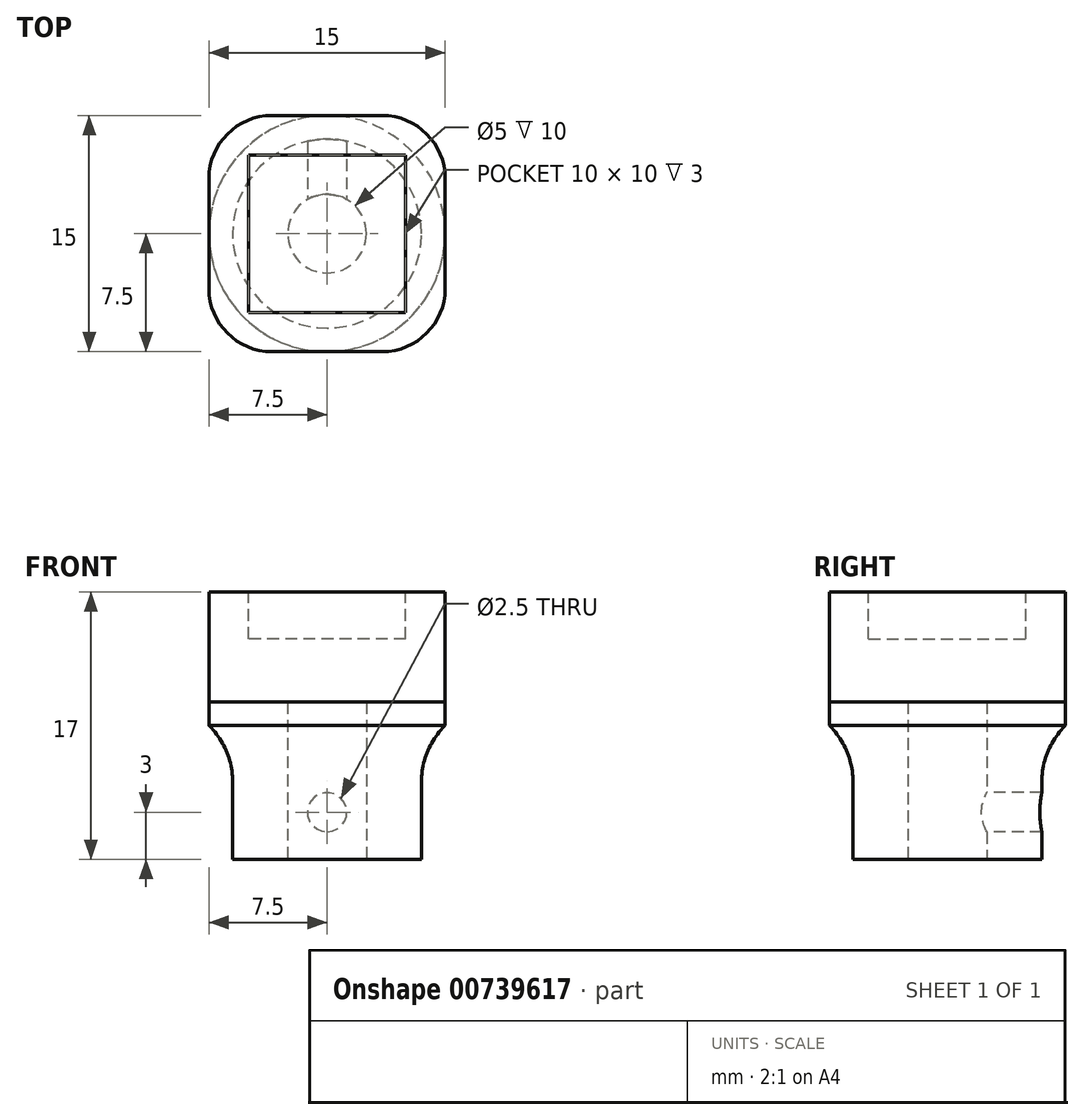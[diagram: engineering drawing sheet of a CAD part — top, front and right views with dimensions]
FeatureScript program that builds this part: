
annotation { "Feature Type Name" : "Feature", "Feature Type Description" : "" }
export const myFeature = defineFeature(function(context is Context, id is Id, definition is map)
    precondition{}
    {
        {
            var Q0;
            Q0=qCreatedBy(makeId("Top.planeOp"),FACE);
            var sketch = newSketch(context, id + "F0", { "sketchPlane" : qUnion([Q0])});
            skCircle(sketch, "E0", {"center": v(0, 0) * mm, "radius": 2.5 * mm});
            skCircle(sketch, "E1", {"center": v(0, 0) * mm, "radius": 6 * mm});
            skSolve(sketch);
        }
        {
            var Q0;
            Q0=qSketchRegion(id+"F0",true);
            extrude(context, id + "F1", {"entities" : qUnion([Q0]), "depth" : 10 * mm});
        }
        {
            var Q0;
            Q0=makeQuery(id+"F1.opExtrude","CAP_FACE",FACE,{"disambiguationData":[OSD([sQuery(id+"F0.wireOp",EDGE,"E0"),sQuery(id+"F0.wireOp",EDGE,"E1")])],"isStart":false});
            var sketch = newSketch(context, id + "F2", { "sketchPlane" : qUnion([Q0])});
            skLineSegment(sketch, "E2.bottom", {"start": v(7.5, -7.5) * mm, "end": v(-7.5, -7.5) * mm});
            skLineSegment(sketch, "E2.top", {"start": v(7.5, 7.5) * mm, "end": v(-7.5, 7.5) * mm});
            skLineSegment(sketch, "E2.left", {"start": v(7.5, -7.5) * mm, "end": v(7.5, 7.5) * mm});
            skLineSegment(sketch, "E2.right", {"start": v(-7.5, -7.5) * mm, "end": v(-7.5, 7.5) * mm});
            skPoint(sketch, "E2.middle", {"position": v(0, 0) * mm});
            skSolve(sketch);
        }
        {
            var Q0;
            Q0=qSketchRegion(id+"F2",true);
            extrude(context, id + "F3", {"entities" : qUnion([Q0]), "operationType" : NewBodyOperationType.ADD, "depth" : 7 * mm});
        }
        {
            var Q0;
            Q0=makeQuery(id+"F3.opExtrude","CAP_FACE",FACE,{"disambiguationData":[OSD([sQuery(id+"F2.wireOp",EDGE,"E2.bottom"),sQuery(id+"F2.wireOp",EDGE,"E2.top"),sQuery(id+"F2.wireOp",EDGE,"E2.left"),sQuery(id+"F2.wireOp",EDGE,"E2.right")])],"isStart":false});
            var sketch = newSketch(context, id + "F4", { "sketchPlane" : qUnion([Q0])});
            skLineSegment(sketch, "E3.bottom", {"start": v(5, -5) * mm, "end": v(-5, -5) * mm});
            skLineSegment(sketch, "E3.top", {"start": v(5, 5) * mm, "end": v(-5, 5) * mm});
            skLineSegment(sketch, "E3.left", {"start": v(5, -5) * mm, "end": v(5, 5) * mm});
            skLineSegment(sketch, "E3.right", {"start": v(-5, -5) * mm, "end": v(-5, 5) * mm});
            skPoint(sketch, "E3.middle", {"position": v(0, 0) * mm});
            skSolve(sketch);
        }
        {
            var Q0;
            Q0=qSketchRegion(id+"F4",true);
            extrude(context, id + "F5", {"entities" : qUnion([Q0]), "operationType" : NewBodyOperationType.REMOVE, "oppositeDirection" : true, "depth" : 3 * mm});
        }
        {
            var Q0;
            Q0=makeQuery(id+"F3.opExtrude","SWEPT_EDGE",EDGE,{"disambiguationData":[OSD([sQuery(id+"F2.wireOp",EDGE,"E2.top"),sQuery(id+"F2.wireOp",EDGE,"E2.left")])]});
            var Q1;
            Q1=makeQuery(id+"F3.opExtrude","SWEPT_EDGE",EDGE,{"disambiguationData":[OSD([sQuery(id+"F2.wireOp",EDGE,"E2.bottom"),sQuery(id+"F2.wireOp",EDGE,"E2.left")])]});
            var Q2;
            Q2=makeQuery(id+"F3.opExtrude","SWEPT_EDGE",EDGE,{"disambiguationData":[OSD([sQuery(id+"F2.wireOp",EDGE,"E2.bottom"),sQuery(id+"F2.wireOp",EDGE,"E2.right")])]});
            var Q3;
            Q3=makeQuery(id+"F3.opExtrude","SWEPT_EDGE",EDGE,{"disambiguationData":[OSD([sQuery(id+"F2.wireOp",EDGE,"E2.top"),sQuery(id+"F2.wireOp",EDGE,"E2.right")])]});
            fillet(context, id + "F6", {"entities" : qUnion([Q0, Q1, Q2, Q3]), "radius" : 4 * mm, "tangentPropagation" : true, "allowEdgeOverflow" : false});
        }
        {
            var Q0;
            {var subQ0=sQuery(id+"F2.wireOp",EDGE,"E2.left");var subQ1=sQuery(id+"F2.wireOp",EDGE,"E2.top");var subQ2=sQuery(id+"F2.wireOp",EDGE,"E2.bottom");var subQ3=sQuery(id+"F2.wireOp",EDGE,"E2.right");Q0=makeQuery(id+"F3.boolean.opBoolean","SPLIT",FACE,{"disambiguationData":[TD([makeQuery(id+"F1.opExtrude","SWEPT_FACE",FACE,{"disambiguationData":[OSD([sQuery(id+"F0.wireOp",EDGE,"E1")])]})])],"derivedFrom":makeQuery(id+"F3.opExtrude","CAP_FACE",FACE,{"disambiguationData":[OSD([subQ2,subQ1,subQ0,subQ3])],"isStart":true})});}
            var sketch = newSketch(context, id + "F7", { "sketchPlane" : qUnion([Q0])});
            skCircle(sketch, "E4", {"center": v(0, 0) * mm, "radius": 6 * mm});
            skCircle(sketch, "E5", {"center": v(0, 0) * mm, "radius": 7.5 * mm});
            skSolve(sketch);
        }
        {
            var Q0;
            Q0=qSketchRegion(id+"F7",true);
            extrude(context, id + "F8", {"entities" : qUnion([Q0]), "operationType" : NewBodyOperationType.ADD, "depth" : 3 * mm});
        }
        {
            var Q0;
            Q0=makeQuery(id+"F8.opExtrude","CAP_EDGE",EDGE,{"disambiguationData":[OSD([sQuery(id+"F7.wireOp",EDGE,"E5")])],"isStart":false});
            chamfer(context, id + "F9", {"entities" : qUnion([Q0]), "width" : 1.5 * mm, "tangentPropagation" : true});
        }
        {
            var Q0;
            Q0=makeQuery(id+"F8.opExtrude","CAP_EDGE",EDGE,{"disambiguationData":[OSD([sQuery(id+"F7.wireOp",EDGE,"E4")])],"isStart":false});
            var Q1;
            Q1=makeQuery(id+"F9.opChamfer","BLEND_EDGE",EDGE,{"blendedFrom":[makeQuery(id+"F8.opExtrude","CAP_EDGE",EDGE,{"disambiguationData":[OSD([sQuery(id+"F7.wireOp",EDGE,"E5")])],"isStart":false}),makeQuery(id+"F1.opExtrude","SWEPT_FACE",FACE,{"disambiguationData":[OSD([sQuery(id+"F0.wireOp",EDGE,"E1")])]})],"blendedInto":[makeQuery(id+"F1.opExtrude","SWEPT_FACE",FACE,{"disambiguationData":[OSD([sQuery(id+"F0.wireOp",EDGE,"E1")])]})]});
            fillet(context, id + "F10", {"entities" : qUnion([Q0, Q1]), "radius" : 5 * mm, "tangentPropagation" : true, "allowEdgeOverflow" : false});
        }
        {
            var Q0;
            Q0=qCreatedBy(makeId("Front.planeOp"),FACE);
            var sketch = newSketch(context, id + "F11", { "sketchPlane" : qUnion([Q0])});
            skCircle(sketch, "E6", {"center": v(0, 3) * mm, "radius": 1.25 * mm});
            skSolve(sketch);
        }
        {
            var Q0;
            Q0=qSketchRegion(id+"F11",true);
            extrude(context, id + "F12", {"entities" : qUnion([Q0]), "operationType" : NewBodyOperationType.REMOVE, "oppositeDirection" : true, "depth" : 10 * mm});
        }
    });
